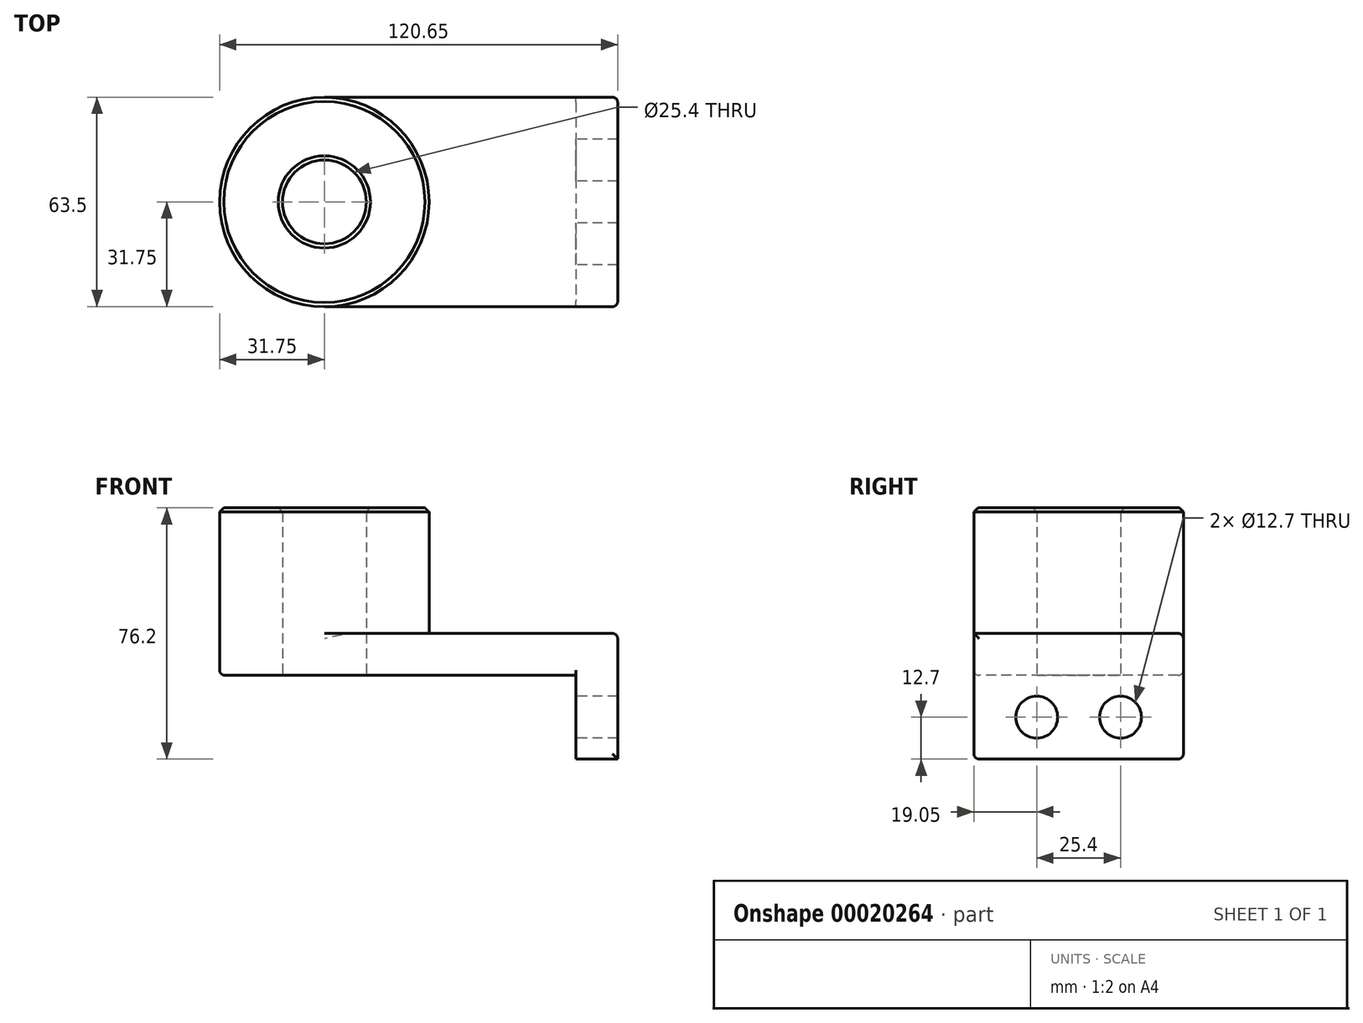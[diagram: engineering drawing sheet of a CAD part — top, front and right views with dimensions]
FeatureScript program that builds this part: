
annotation { "Feature Type Name" : "Feature", "Feature Type Description" : "" }
export const myFeature = defineFeature(function(context is Context, id is Id, definition is map)
    precondition{}
    {
        {
            var Q0;
            Q0=qCreatedBy(makeId("Top.planeOp"),FACE);
            var sketch = newSketch(context, id + "F0", { "sketchPlane" : qUnion([Q0])});
            skLineSegment(sketch, "E0.rect.bottom", {"start": v(-38.1, 31.75) * mm, "end": v(38.1, 31.75) * mm});
            skLineSegment(sketch, "E0.rect.top", {"start": v(-38.1, -31.75) * mm, "end": v(38.1, -31.75) * mm});
            skLineSegment(sketch, "E0.rect.left", {"start": v(-38.1, 31.75) * mm, "end": v(-38.1, -31.75) * mm});
            skLineSegment(sketch, "E0.rect.right", {"start": v(38.1, 31.75) * mm, "end": v(38.1, -31.75) * mm});
            skPoint(sketch, "E0.rect.middle", {"position": v(0, 0) * mm});
            skCircle(sketch, "E1", {"center": v(-38.1, 0) * mm, "radius": 31.75 * mm});
            skCircle(sketch, "E2", {"center": v(-38.1, 0) * mm, "radius": 12.7 * mm});
            skSolve(sketch);
        }
        {
            var Q0;
            Q0 = qSketchRegion(id + "F0", true);
            extrude(context, id + "F1", {"entities" : qUnion([Q0]), "depth" : 12.7 * mm});
        }
        {
            var Q0;
            {var subQ0=sQuery(id+"F0.wireOp",EDGE,"E2");var subQ1=sQuery(id+"F0.wireOp",EDGE,"E0.rect.left");var subQ3=makeQuery(id+"F0.imprint","INTERSECT",VERTEX,{"disambiguationData":[OD(0.0)],"derivedFrom":[subQ1,subQ0]});Q0=makeQuery(id+"F0.imprint","IMPRINT",FACE,{"disambiguationData":[TD([[makeQuery(id+"F0.imprint","IMPRINT",EDGE,{"disambiguationData":[TD([[subQ3,-1.0]])],"derivedFrom":subQ0}),-1.0]])]});}
            var Q1;
            {var subQ0=sQuery(id+"F0.wireOp",EDGE,"E2");var subQ1=sQuery(id+"F0.wireOp",EDGE,"E0.rect.left");var subQ3=makeQuery(id+"F0.imprint","INTERSECT",VERTEX,{"disambiguationData":[OD(0.0)],"derivedFrom":[subQ1,subQ0]});Q1=makeQuery(id+"F0.imprint","IMPRINT",FACE,{"disambiguationData":[TD([[makeQuery(id+"F0.imprint","IMPRINT",EDGE,{"disambiguationData":[TD([[subQ3,1.0]])],"derivedFrom":subQ0}),-1.0]])]});}
            extrude(context, id + "F2", {"entities" : qUnion([Q0, Q1]), "operationType" : NewBodyOperationType.ADD, "depth" : 50.8 * mm});
        }
        {
            var Q0;
            Q0=makeQuery(id+"F1.opExtrude","SWEPT_FACE",FACE,{"disambiguationData":[OSD([sQuery(id+"F0.wireOp",EDGE,"E0.rect.right")])]});
            var sketch = newSketch(context, id + "F3", { "sketchPlane" : qUnion([Q0])});
            skLineSegment(sketch, "E3.bottom", {"start": v(-31.75, 12.7) * mm, "end": v(31.75, 12.7) * mm});
            skLineSegment(sketch, "E3.top", {"start": v(-31.75, -25.4) * mm, "end": v(31.75, -25.4) * mm});
            skLineSegment(sketch, "E3.left", {"start": v(-31.75, 12.7) * mm, "end": v(-31.75, -25.4) * mm});
            skLineSegment(sketch, "E3.right", {"start": v(31.75, 12.7) * mm, "end": v(31.75, -25.4) * mm});
            skCircle(sketch, "E4", {"center": v(-12.7, -12.7) * mm, "radius": 6.35 * mm});
            skLineSegment(sketch, "E5", {"start": v(0, 0) * mm, "end": v(0, -25.4) * mm, "construction": true});
            skCircle(sketch, "E6.MirrorC", {"center": v(12.7, -12.7) * mm, "radius": 6.35 * mm});
            skSolve(sketch);
        }
        {
            var Q0;
            {var subQ2=sQuery(id+"F3.wireOp",EDGE,"E3.top");Q0=makeQuery(id+"F3.imprint","IMPRINT",FACE,{"disambiguationData":[TD([[makeQuery(id+"F3.imprint","IMPRINT",EDGE,{"derivedFrom":subQ2}),1.0]])]});}
            var Q1;
            {var subQ2=sQuery(id+"F3.wireOp",EDGE,"E3.bottom");Q1=makeQuery(id+"F3.imprint","IMPRINT",FACE,{"disambiguationData":[TD([[makeQuery(id+"F3.imprint","IMPRINT",EDGE,{"derivedFrom":subQ2}),1.0]])]});}
            extrude(context, id + "F4", {"entities" : qUnion([Q0, Q1]), "operationType" : NewBodyOperationType.ADD, "depth" : 12.7 * mm});
        }
        {
            var Q0;
            Q0=makeQuery(id+"F4.opExtrude","CAP_EDGE",EDGE,{"disambiguationData":[OSD([sQuery(id+"F3.wireOp",EDGE,"E3.bottom")])],"isStart":false});
            var Q1;
            Q1=makeQuery(id+"F4.opExtrude","SWEPT_EDGE",EDGE,{"disambiguationData":[OSD([sQuery(id+"F3.wireOp",EDGE,"E3.top"),sQuery(id+"F3.wireOp",EDGE,"E3.left")])]});
            var Q2;
            Q2=makeQuery(id+"F4.opExtrude","SWEPT_EDGE",EDGE,{"disambiguationData":[OSD([sQuery(id+"F3.wireOp",EDGE,"E3.top"),sQuery(id+"F3.wireOp",EDGE,"E3.right")])]});
            var Q3;
            Q3=makeQuery(id+"F4.boolean.opBoolean","MERGE",EDGE,{"derivedFrom":[makeQuery(id+"F1.opExtrude","CAP_EDGE",EDGE,{"disambiguationData":[OSD([sQuery(id+"F0.wireOp",EDGE,"E0.rect.bottom")])],"isStart":false}),makeQuery(id+"F4.opExtrude","SWEPT_EDGE",EDGE,{"disambiguationData":[OSD([sQuery(id+"F3.wireOp",EDGE,"E3.bottom"),sQuery(id+"F3.wireOp",EDGE,"E3.right")])]})]});
            var Q4;
            Q4=makeQuery(id+"F4.opExtrude","CAP_EDGE",EDGE,{"disambiguationData":[OSD([sQuery(id+"F3.wireOp",EDGE,"E3.left")])],"isStart":false});
            var Q5;
            Q5=makeQuery(id+"F4.opExtrude","CAP_EDGE",EDGE,{"disambiguationData":[OSD([sQuery(id+"F3.wireOp",EDGE,"E3.right")])],"isStart":false});
            var Q6;
            Q6=makeQuery(id+"F1.opExtrude","CAP_EDGE",EDGE,{"disambiguationData":[OSD([sQuery(id+"F0.wireOp",EDGE,"E0.rect.top")])],"isStart":true});
            var Q7;
            Q7=makeQuery(id+"F1.opExtrude","CAP_EDGE",EDGE,{"disambiguationData":[OSD([sQuery(id+"F0.wireOp",EDGE,"E0.rect.bottom")])],"isStart":true});
            var Q8;
            Q8=makeQuery(id+"F1.opExtrude","CAP_EDGE",EDGE,{"disambiguationData":[OSD([sQuery(id+"F0.wireOp",EDGE,"E0.rect.right")])],"isStart":true});
            fillet(context, id + "F5", {"entities" : qUnion([Q0, Q1, Q2, Q3, Q4, Q5, Q6, Q7, Q8]), "radius" : 1.59 * mm, "tangentPropagation" : true, "allowEdgeOverflow" : false});
        }
        {
            var Q0;
            Q0=makeQuery(id+"F2.opExtrude","CAP_FACE",FACE,{"disambiguationData":[OSD([sQuery(id+"F0.wireOp",EDGE,"E1"),sQuery(id+"F0.wireOp",EDGE,"E2")])],"isStart":false});
            chamfer(context, id + "F6", {"entities" : qUnion([Q0]), "width" : 1.27 * mm, "tangentPropagation" : true});
        }
    });
